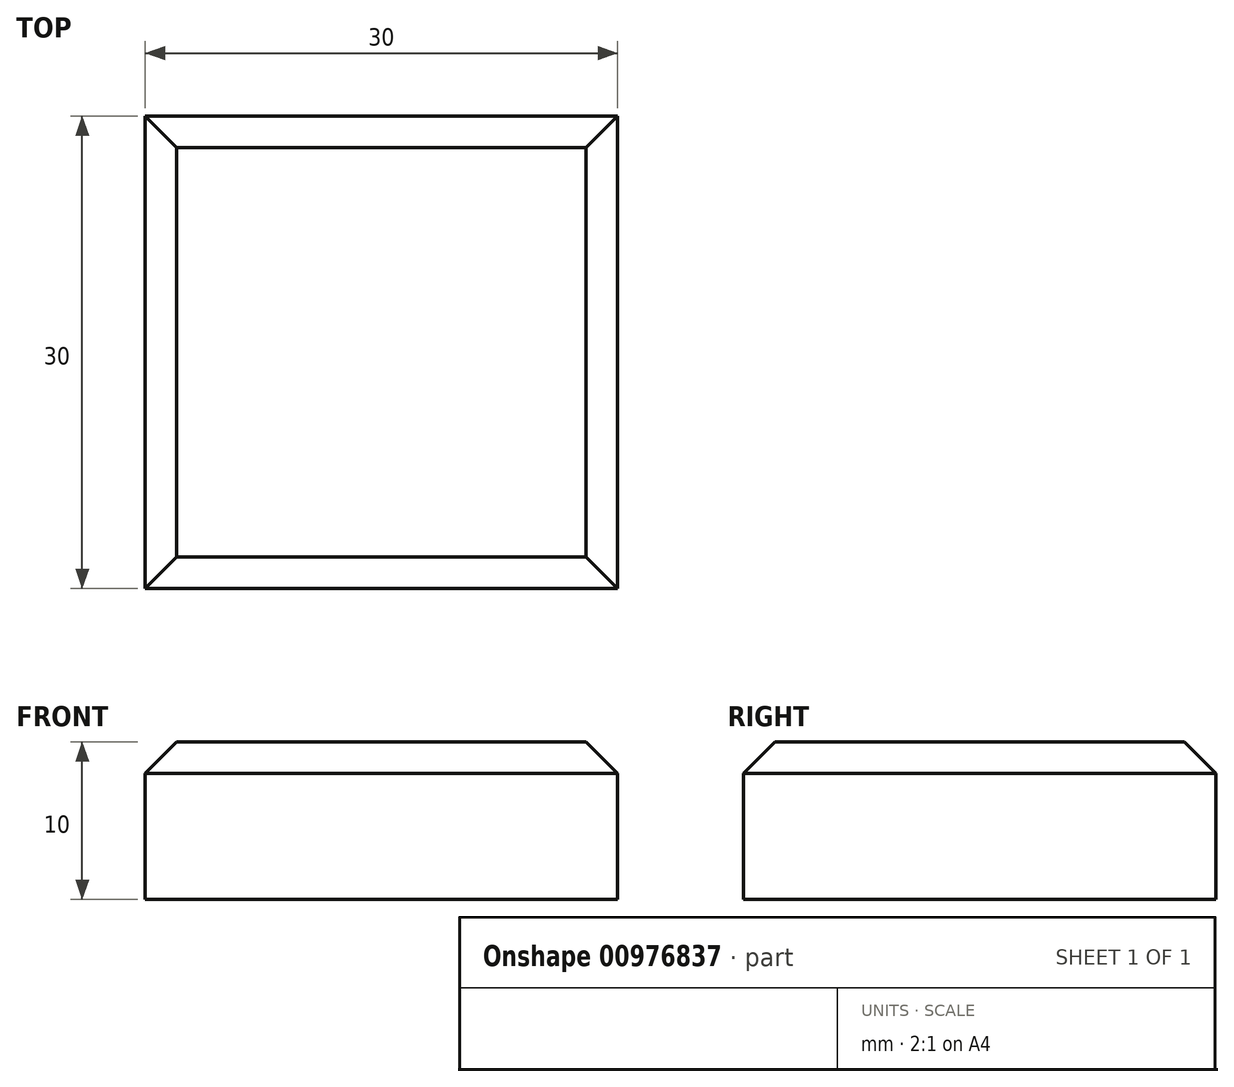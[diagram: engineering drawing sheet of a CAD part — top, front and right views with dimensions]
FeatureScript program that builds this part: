
annotation { "Feature Type Name" : "Feature", "Feature Type Description" : "" }
export const myFeature = defineFeature(function(context is Context, id is Id, definition is map)
    precondition{}
    {
        {
            var Q0;
            Q0=qCreatedBy(makeId("Top.planeOp"),FACE);
            var sketch = newSketch(context, id + "F0", { "sketchPlane" : qUnion([Q0])});
            skLineSegment(sketch, "E0.bottom", {"start": v(-12.33, 15.72) * mm, "end": v(17.67, 15.72) * mm});
            skLineSegment(sketch, "E0.top", {"start": v(-12.33, -14.28) * mm, "end": v(17.67, -14.28) * mm});
            skLineSegment(sketch, "E0.left", {"start": v(-12.33, 15.72) * mm, "end": v(-12.33, -14.28) * mm});
            skLineSegment(sketch, "E0.right", {"start": v(17.67, 15.72) * mm, "end": v(17.67, -14.28) * mm});
            skSolve(sketch);
        }
        {
            var Q0;
            Q0=makeQuery(id+"F0.imprint","IMPRINT",FACE,{"disambiguationData":[TD([[makeQuery(id+"F0.imprint","IMPRINT",EDGE,{"derivedFrom":sQuery(id+"F0.wireOp",EDGE,"E0.bottom")}),-1.0]])]});
            extrude(context, id + "F1", {"entities" : qUnion([Q0]), "depth" : 10 * mm, "offsetDistance" : 25.4 * mm});
        }
        {
            var Q0;
            Q0=makeQuery(id+"F1.opExtrude","CAP_EDGE",EDGE,{"disambiguationData":[OSD([sQuery(id+"F0.wireOp",EDGE,"E0.top")])],"isStart":false});
            var Q1;
            Q1=makeQuery(id+"F1.opExtrude","CAP_EDGE",EDGE,{"disambiguationData":[OSD([sQuery(id+"F0.wireOp",EDGE,"E0.right")])],"isStart":false});
            var Q2;
            Q2=makeQuery(id+"F1.opExtrude","CAP_EDGE",EDGE,{"disambiguationData":[OSD([sQuery(id+"F0.wireOp",EDGE,"E0.bottom")])],"isStart":false});
            var Q3;
            Q3=makeQuery(id+"F1.opExtrude","CAP_EDGE",EDGE,{"disambiguationData":[OSD([sQuery(id+"F0.wireOp",EDGE,"E0.left")])],"isStart":false});
            chamfer(context, id + "F2", {"entities" : qUnion([Q0, Q1, Q2, Q3]), "width" : 2 * mm, "tangentPropagation" : true});
        }
    });
